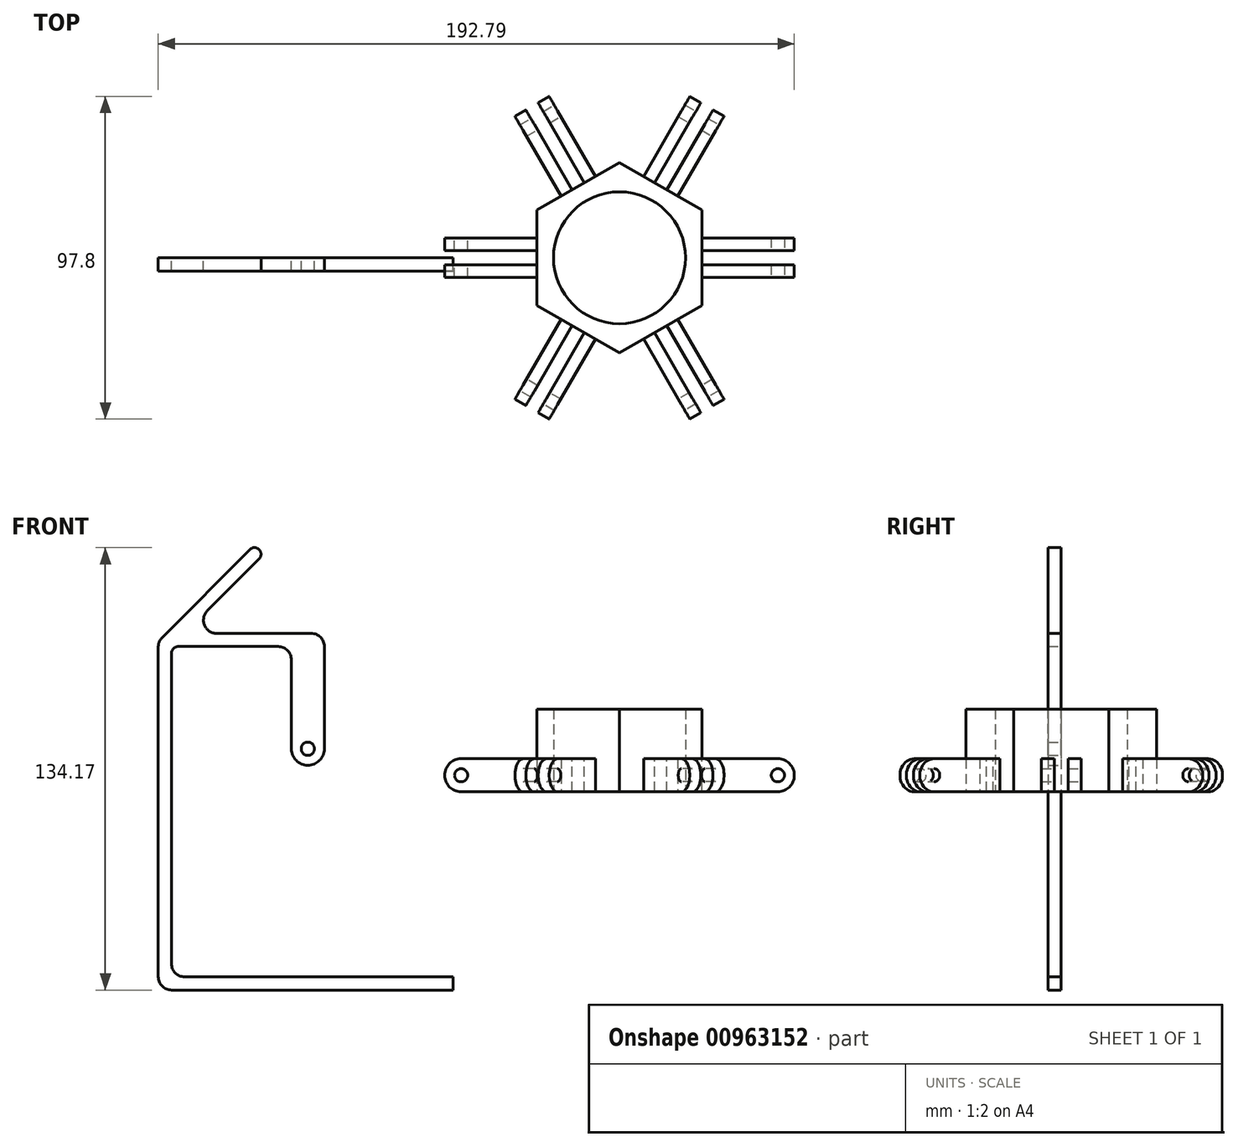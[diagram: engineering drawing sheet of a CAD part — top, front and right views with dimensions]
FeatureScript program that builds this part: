
annotation { "Feature Type Name" : "Feature", "Feature Type Description" : "" }
export const myFeature = defineFeature(function(context is Context, id is Id, definition is map)
    precondition{}
    {
        {
            var Q0;
            Q0=qCreatedBy(makeId("Front.planeOp"),FACE);
            var sketch = newSketch(context, id + "F0", { "sketchPlane" : qUnion([Q0])});
            skLineSegment(sketch, "E0", {"start": v(-139.79, -56.14) * mm, "end": v(-139.79, 43.94) * mm});
            skLineSegment(sketch, "E1", {"start": v(-99.45, 13.02) * mm, "end": v(-99.45, 40.02) * mm});
            skLineSegment(sketch, "E2", {"start": v(-103.45, 44.02) * mm, "end": v(-133.79, 44.02) * mm});
            skLineSegment(sketch, "E3", {"start": v(-135.79, 42.02) * mm, "end": v(-135.79, -52.14) * mm});
            skPoint(sketch, "E4.middle", {"position": v(0, 0) * mm});
            skPoint(sketch, "E5.visualSharp", {"position": v(-99.45, 18.02) * mm});
            skPoint(sketch, "E6.visualSharp", {"position": v(-99.45, 8.02) * mm});
            skArc(sketch, "E7.filletArc", {"start": v(-99.45, 13.02) * mm, "mid": v(-97.99, 9.49) * mm, "end": v(-94.45, 8.02) * mm});
            skCircle(sketch, "E8", {"center": v(-94.45, 13.02) * mm, "radius": 2 * mm});
            skPoint(sketch, "E9.visualSharp", {"position": v(-135.79, 44.02) * mm});
            skArc(sketch, "E9.filletArc", {"start": v(-133.79, 44.02) * mm, "mid": v(-135.2, 43.44) * mm, "end": v(-135.79, 42.02) * mm});
            skPoint(sketch, "E10.visualSharp", {"position": v(-99.45, 44.02) * mm});
            skArc(sketch, "E10.filletArc", {"start": v(-99.45, 40.02) * mm, "mid": v(-100.62, 42.85) * mm, "end": v(-103.45, 44.02) * mm});
            skLineSegment(sketch, "E11", {"start": v(-50.45, -56.14) * mm, "end": v(-131.79, -56.14) * mm});
            skLineSegment(sketch, "E12", {"start": v(-135.79, -60.14) * mm, "end": v(-50.45, -60.14) * mm});
            skPoint(sketch, "E13.visualSharp", {"position": v(-139.79, -60.14) * mm});
            skArc(sketch, "E13.filletArc", {"start": v(-139.79, -56.14) * mm, "mid": v(-138.61, -58.97) * mm, "end": v(-135.79, -60.14) * mm});
            skArc(sketch, "E14.filletArc", {"start": v(-135.79, -52.14) * mm, "mid": v(-134.61, -54.97) * mm, "end": v(-131.79, -56.14) * mm});
            skLineSegment(sketch, "E15", {"start": v(-138.62, 46.76) * mm, "end": v(-112.06, 73.44) * mm});
            skLineSegment(sketch, "E16", {"start": v(-109.23, 73.45) * mm, "end": v(-109.23, 73.45) * mm});
            skLineSegment(sketch, "E17", {"start": v(-109.23, 70.62) * mm, "end": v(-124.93, 54.85) * mm});
            skLineSegment(sketch, "E18", {"start": v(-122.1, 48.02) * mm, "end": v(-93.45, 48.02) * mm});
            skPoint(sketch, "E19.visualSharp", {"position": v(-139.79, 45.59) * mm});
            skArc(sketch, "E19.filletArc", {"start": v(-138.62, 46.76) * mm, "mid": v(-139.48, 45.46) * mm, "end": v(-139.79, 43.94) * mm});
            skPoint(sketch, "E20.visualSharp", {"position": v(-131.72, 48.02) * mm});
            skArc(sketch, "E20.filletArc", {"start": v(-124.93, 54.85) * mm, "mid": v(-125.78, 50.49) * mm, "end": v(-122.1, 48.02) * mm});
            skPoint(sketch, "E21.visualSharp", {"position": v(-89.45, 48.02) * mm});
            skArc(sketch, "E21.filletArc", {"start": v(-89.45, 44.02) * mm, "mid": v(-90.62, 46.85) * mm, "end": v(-93.45, 48.02) * mm});
            skPoint(sketch, "E22.visualSharp", {"position": v(-110.65, 74.86) * mm});
            skArc(sketch, "E22.filletArc", {"start": v(-109.23, 73.45) * mm, "mid": v(-110.65, 74.03) * mm, "end": v(-112.06, 73.44) * mm});
            skPoint(sketch, "E23.visualSharp", {"position": v(-107.82, 72.04) * mm});
            skArc(sketch, "E23.filletArc", {"start": v(-109.23, 70.62) * mm, "mid": v(-108.65, 72.04) * mm, "end": v(-109.23, 73.45) * mm});
            skLineSegment(sketch, "E24", {"start": v(-94.45, 8.02) * mm, "end": v(-94.45, 8.02) * mm});
            skPoint(sketch, "E25.visualSharp", {"position": v(-89.45, 8.02) * mm});
            skArc(sketch, "E25.filletArc", {"start": v(-94.45, 8.02) * mm, "mid": v(-90.92, 9.49) * mm, "end": v(-89.45, 13.02) * mm});
            skLineSegment(sketch, "E26", {"start": v(-89.45, 44.02) * mm, "end": v(-89.45, 13.02) * mm});
            skLineSegment(sketch, "E27", {"start": v(-50.45, -56.14) * mm, "end": v(-50.45, -60.14) * mm});
            skSolve(sketch);
        }
        {
            var Q0;
            Q0 = qSketchRegion(id + "F0", true);
            extrude(context, id + "F1", {"entities" : qUnion([Q0]), "depth" : 4 * mm, "offsetDistance" : 25 * mm});
        }
        {
            var Q0;
            Q0=qCreatedBy(makeId("Front.planeOp"),FACE);
            var sketch = newSketch(context, id + "F2", { "sketchPlane" : qUnion([Q0])});
            skLineSegment(sketch, "E28", {"start": v(0, 0) * mm, "end": v(0, 25.86) * mm, "construction": true});
            skLineSegment(sketch, "E29.bottom", {"start": v(-48, 10) * mm, "end": v(-25, 10) * mm});
            skLineSegment(sketch, "E29.top", {"start": v(-48, 0) * mm, "end": v(-25, 0) * mm});
            skLineSegment(sketch, "E29.left", {"start": v(-53, 5) * mm, "end": v(-53, 5) * mm});
            skLineSegment(sketch, "E29.right", {"start": v(-25, 10) * mm, "end": v(-25, 0) * mm});
            skCircle(sketch, "E30", {"center": v(-48, 5) * mm, "radius": 2 * mm});
            skPoint(sketch, "E31.visualSharp", {"position": v(-53, 10) * mm});
            skArc(sketch, "E31.filletArc", {"start": v(-48, 10) * mm, "mid": v(-51.54, 8.54) * mm, "end": v(-53, 5) * mm});
            skPoint(sketch, "E32.visualSharp", {"position": v(-53, 0) * mm});
            skArc(sketch, "E32.filletArc", {"start": v(-53, 5) * mm, "mid": v(-51.54, 1.46) * mm, "end": v(-48, 0) * mm});
            skSolve(sketch);
        }
        {
            var Q0;
            Q0 = qSketchRegion(id + "F2", true);
            extrude(context, id + "F3", {"entities" : qUnion([Q0]), "endBound" : BoundingType.SYMMETRIC, "depth" : 12 * mm, "offsetDistance" : 25 * mm});
        }
        {
            var Q0;
            Q0=makeQuery(id+"F3.opExtrude","SWEPT_FACE",FACE,{"disambiguationData":[OSD([sQuery(id+"F2.wireOp",EDGE,"E29.bottom")])]});
            var sketch = newSketch(context, id + "F4", { "sketchPlane" : qUnion([Q0])});
            skLineSegment(sketch, "E33.bottom", {"start": v(-53, 2.15) * mm, "end": v(-25, 2.15) * mm});
            skLineSegment(sketch, "E33.top", {"start": v(-53, -2.15) * mm, "end": v(-25, -2.15) * mm});
            skLineSegment(sketch, "E33.left", {"start": v(-53, 2.15) * mm, "end": v(-53, -2.15) * mm});
            skLineSegment(sketch, "E33.right", {"start": v(-25, 2.15) * mm, "end": v(-25, -2.15) * mm});
            skPoint(sketch, "E34", {"position": v(-53, 0) * mm});
            skSolve(sketch);
        }
        {
            var Q0;
            {var subQ0=sQuery(id+"F4.wireOp",EDGE,"E33.right");Q0=makeQuery(id+"F4.imprint","IMPRINT",FACE,{"disambiguationData":[TD([[makeQuery(id+"F4.imprint","IMPRINT",EDGE,{"derivedFrom":subQ0}),1.0]])]});}
            var Q1;
            {var subQ0=sQuery(id+"F4.wireOp",EDGE,"E33.left");Q1=makeQuery(id+"F4.imprint","IMPRINT",FACE,{"disambiguationData":[TD([[makeQuery(id+"F4.imprint","IMPRINT",EDGE,{"derivedFrom":subQ0}),1.0]])]});}
            extrude(context, id + "F5", {"entities" : qUnion([Q0, Q1]), "operationType" : NewBodyOperationType.REMOVE, "endBound" : BoundingType.UP_TO_NEXT, "oppositeDirection" : true, "depth" : 25 * mm, "offsetDistance" : 25 * mm});
        }
        {
            var Q0;
            Q0=qCreatedBy(makeId("Top.planeOp"),FACE);
            var sketch = newSketch(context, id + "F6", { "sketchPlane" : qUnion([Q0])});
            skCircle(sketch, "E35.cCircle", {"center": v(0, 0) * mm, "radius": 25 * mm, "construction": true});
            skLineSegment(sketch, "E35.0", {"start": v(-25, -14.43) * mm, "end": v(-25, 14.43) * mm});
            skLineSegment(sketch, "E35.1", {"start": v(-25, 14.43) * mm, "end": v(0, 28.87) * mm});
            skLineSegment(sketch, "E35.2", {"start": v(0, 28.87) * mm, "end": v(25, 14.43) * mm});
            skLineSegment(sketch, "E35.3", {"start": v(25, 14.43) * mm, "end": v(25, -14.43) * mm});
            skLineSegment(sketch, "E35.4", {"start": v(25, -14.43) * mm, "end": v(0, -28.87) * mm});
            skLineSegment(sketch, "E35.5", {"start": v(0, -28.87) * mm, "end": v(-25, -14.43) * mm});
            skPoint(sketch, "E35.0.midPoint", {"position": v(-25, 0) * mm});
            skCircle(sketch, "E36", {"center": v(0, 0) * mm, "radius": 20 * mm});
            skSolve(sketch);
        }
        {
            var Q0;
            Q0=makeQuery(id+"F6.imprint","IMPRINT",FACE,{"disambiguationData":[TD([[makeQuery(id+"F6.imprint","IMPRINT",EDGE,{"derivedFrom":sQuery(id+"F6.wireOp",EDGE,"E35.0")}),-1.0]])]});
            var sketch = newSketch(context, id + "F7", { "sketchPlane" : qUnion([Q0])});
            skSolve(sketch);
        }
        {
            var Q0;
            Q0 = qSketchRegion(id + "F7", true);
            var Q1;
            Q1=makeQuery(id+"F7.imprint","IMPRINT",FACE,{"disambiguationData":[TD([[makeQuery(id+"F7.imprint","IMPRINT",EDGE,{"derivedFrom":makeQuery(id+"F6.imprint","IMPRINT",EDGE,{"derivedFrom":sQuery(id+"F6.wireOp",EDGE,"E35.0")})}),-1.0]])]});
            extrude(context, id + "F8", {"entities" : qUnion([Q0, Q1]), "depth" : 25 * mm, "offsetDistance" : 25 * mm});
        }
        {
            var Q0;
            Q0=makeQuery(id+"F5.boolean.opBoolean","SPLIT",BODY,{"disambiguationData":[OD(1.0)],"derivedFrom":makeQuery(id+"F3.opExtrude","SWEPT_BODY",BODY,{"disambiguationData":[OSD([sQuery(id+"F2.wireOp",EDGE,"E29.bottom"),sQuery(id+"F2.wireOp",EDGE,"E29.top"),sQuery(id+"F2.wireOp",EDGE,"E29.right"),sQuery(id+"F2.wireOp",EDGE,"E30"),sQuery(id+"F2.wireOp",EDGE,"E31.filletArc"),sQuery(id+"F2.wireOp",EDGE,"E32.filletArc")])]})});
            var Q1;
            Q1=makeQuery(id+"F5.boolean.opBoolean","SPLIT",BODY,{"disambiguationData":[OD(0.0)],"derivedFrom":makeQuery(id+"F3.opExtrude","SWEPT_BODY",BODY,{"disambiguationData":[OSD([sQuery(id+"F2.wireOp",EDGE,"E29.bottom"),sQuery(id+"F2.wireOp",EDGE,"E29.top"),sQuery(id+"F2.wireOp",EDGE,"E29.right"),sQuery(id+"F2.wireOp",EDGE,"E30"),sQuery(id+"F2.wireOp",EDGE,"E31.filletArc"),sQuery(id+"F2.wireOp",EDGE,"E32.filletArc")])]})});
            var Q2;
            Q2=sQuery(id+"F2.wireOp",EDGE,"E28");
            circularPattern(context, id + "F9", {"operationType" : NewBodyOperationType.ADD, "entities" : qUnion([Q0, Q1]), "axis" : qUnion([Q2]), "angle" : 360 * degree, "instanceCount" : 6, "equalSpace" : true});
        }
    });
